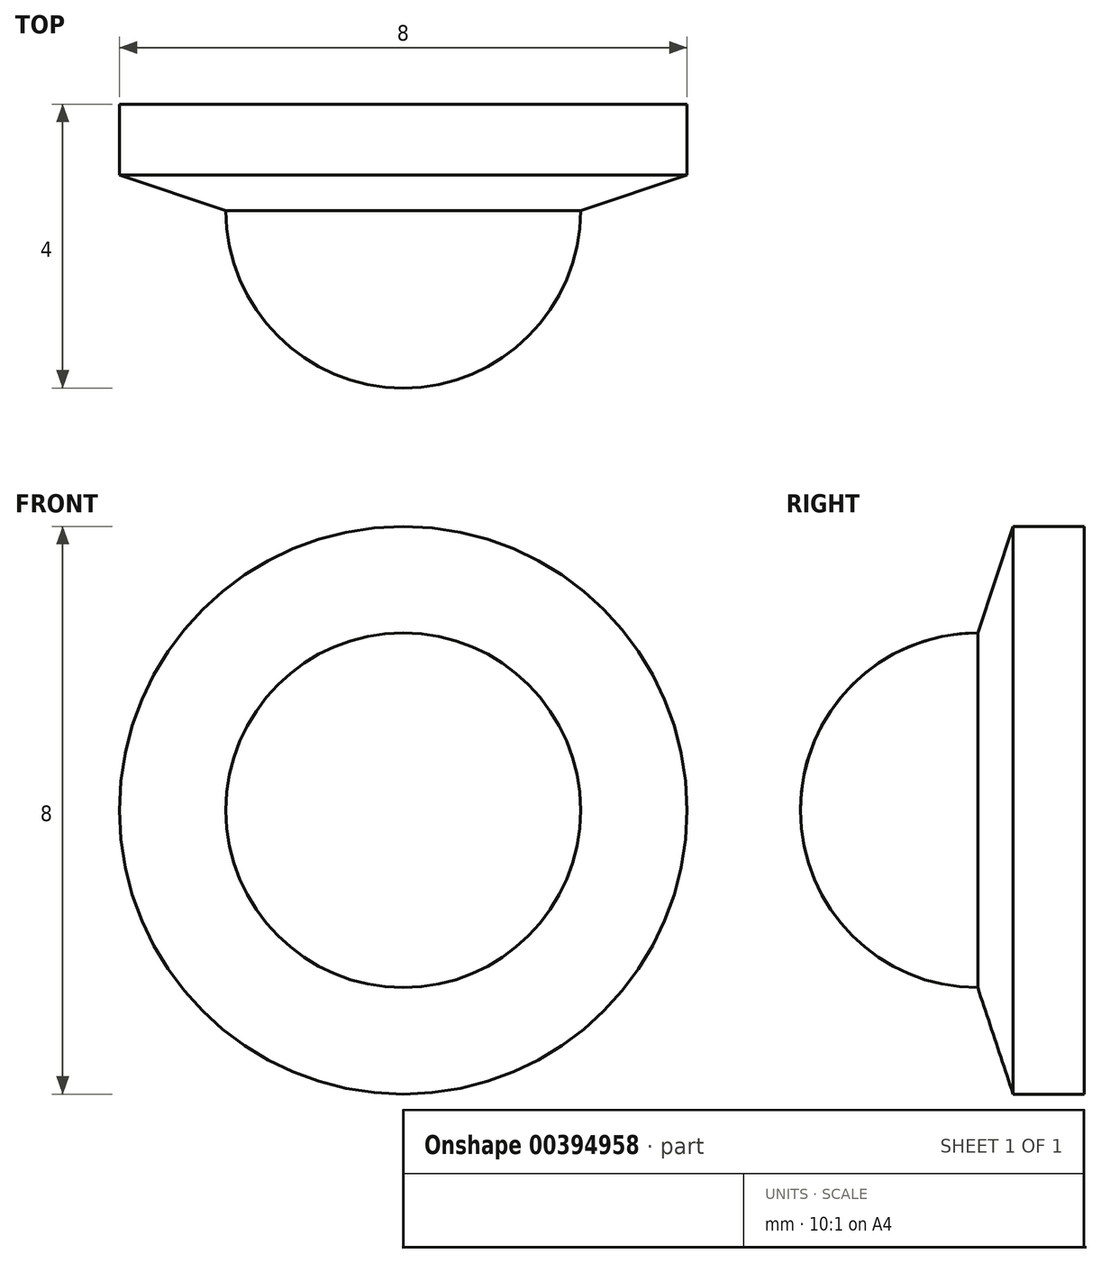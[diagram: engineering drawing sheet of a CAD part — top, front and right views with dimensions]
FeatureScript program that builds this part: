
annotation { "Feature Type Name" : "Feature", "Feature Type Description" : "" }
export const myFeature = defineFeature(function(context is Context, id is Id, definition is map)
    precondition{}
    {
        {
            var Q0;
            Q0=qCreatedBy(makeId("Front.planeOp"),FACE);
            var sketch = newSketch(context, id + "F0", { "sketchPlane" : qUnion([Q0])});
            skCircle(sketch, "E0", {"center": v(0, 0) * mm, "radius": 2.5 * mm});
            skCircle(sketch, "E1", {"center": v(0, 0) * mm, "radius": 4 * mm});
            skSolve(sketch);
        }
        {
            var Q0;
            Q0=qCreatedBy(makeId("Right.planeOp"),FACE);
            var sketch = newSketch(context, id + "F1", { "sketchPlane" : qUnion([Q0])});
            skLineSegment(sketch, "E2.0", {"start": v(0, -4) * mm, "end": v(0, 4) * mm});
            skLineSegment(sketch, "E3.0", {"start": v(0, -2.5) * mm, "end": v(0, 2.5) * mm});
            skLineSegment(sketch, "E4.bottom", {"start": v(0, -2.5) * mm, "end": v(-1.5, -2.5) * mm});
            skLineSegment(sketch, "E4.top", {"start": v(0, 0) * mm, "end": v(-1.5, 0) * mm});
            skLineSegment(sketch, "E4.left", {"start": v(0, -2.5) * mm, "end": v(0, 0) * mm});
            skLineSegment(sketch, "E5", {"start": v(-1.5, 0) * mm, "end": v(-4, 0) * mm});
            skArc(sketch, "E6.trimOffspring", {"start": v(-4, 0) * mm, "mid": v(-3.27, -1.77) * mm, "end": v(-1.5, -2.5) * mm});
            skLineSegment(sketch, "E7", {"start": v(0, 0) * mm, "end": v(0, -2.5) * mm});
            skLineSegment(sketch, "E8", {"start": v(0, -4) * mm, "end": v(-1, -4) * mm});
            skLineSegment(sketch, "E9", {"start": v(-1, -4) * mm, "end": v(-1.5, -2.5) * mm});
            skLineSegment(sketch, "E10", {"start": v(-1.5, 0) * mm, "end": v(0, 0) * mm});
            skSolve(sketch);
        }
        {
            var Q0;
            Q0=makeQuery(id+"F1.imprint","IMPRINT",FACE,{"disambiguationData":[TD([[makeQuery(id+"F1.imprint","IMPRINT",EDGE,{"derivedFrom":sQuery(id+"F1.wireOp",EDGE,"E4.bottom")}),-1.0]])]});
            var Q1;
            {var subQ2=sQuery(id+"F1.wireOp",EDGE,"E4.bottom");Q1=makeQuery(id+"F1.imprint","IMPRINT",FACE,{"disambiguationData":[TD([[makeQuery(id+"F1.imprint","IMPRINT",EDGE,{"derivedFrom":subQ2}),1.0]])]});}
            var Q2;
            Q2=sQuery(id+"F1.wireOp",EDGE,"E10");
            revolve(context, id + "F2", {"entities" : qUnion([Q0, Q1]), "axis" : qUnion([Q2]), "revolveType" : RevolveType.FULL});
        }
    });
